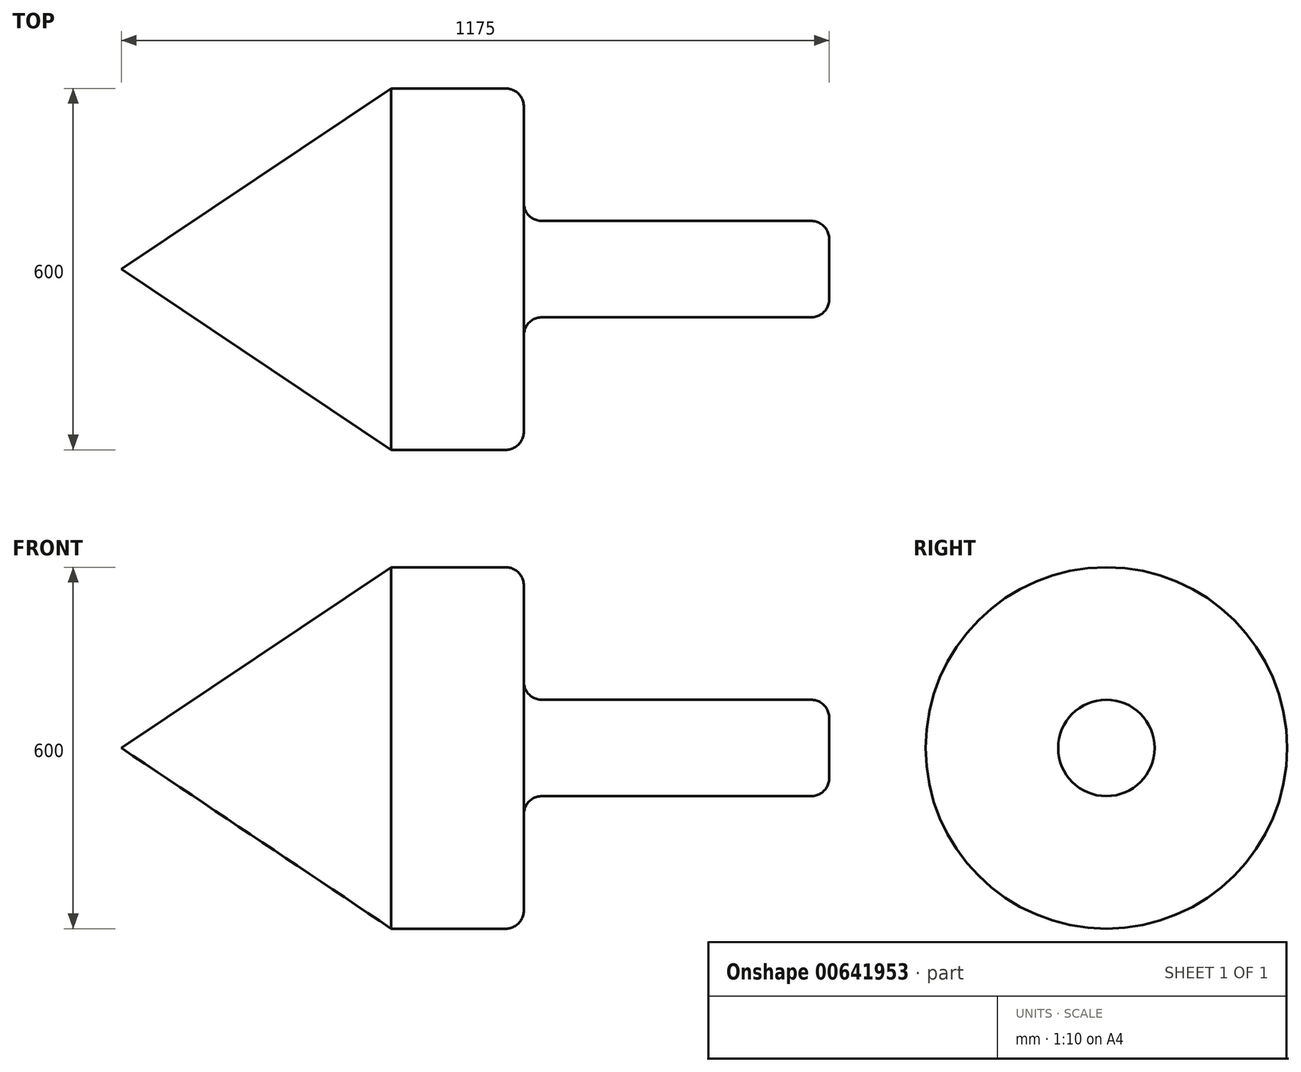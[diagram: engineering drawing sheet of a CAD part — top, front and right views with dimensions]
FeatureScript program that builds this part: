
annotation { "Feature Type Name" : "Feature", "Feature Type Description" : "" }
export const myFeature = defineFeature(function(context is Context, id is Id, definition is map)
    precondition{}
    {
        {
            var Q0;
            Q0=qCreatedBy(makeId("Front.planeOp"),FACE);
            var sketch = newSketch(context, id + "F0", { "sketchPlane" : qUnion([Q0])});
            skLineSegment(sketch, "E0", {"start": v(579.21, 0) * mm, "end": v(-595.79, 0) * mm});
            skLineSegment(sketch, "E1", {"start": v(579.21, 0) * mm, "end": v(579.21, 50) * mm});
            skLineSegment(sketch, "E2", {"start": v(549.21, 80) * mm, "end": v(102.21, 80) * mm});
            skLineSegment(sketch, "E3", {"start": v(72.21, 110) * mm, "end": v(72.21, 270) * mm});
            skLineSegment(sketch, "E4", {"start": v(42.21, 300) * mm, "end": v(-147.79, 300) * mm});
            skLineSegment(sketch, "E5", {"start": v(-147.79, 300) * mm, "end": v(-595.79, 0) * mm});
            skPoint(sketch, "E6.visualSharp", {"position": v(72.21, 300) * mm});
            skArc(sketch, "E6.filletArc", {"start": v(72.21, 270) * mm, "mid": v(63.43, 291.21) * mm, "end": v(42.21, 300) * mm});
            skPoint(sketch, "E7.visualSharp", {"position": v(72.21, 80) * mm});
            skArc(sketch, "E7.filletArc", {"start": v(72.21, 110) * mm, "mid": v(81, 88.79) * mm, "end": v(102.21, 80) * mm});
            skPoint(sketch, "E8.visualSharp", {"position": v(579.21, 80) * mm});
            skArc(sketch, "E8.filletArc", {"start": v(579.21, 50) * mm, "mid": v(570.43, 71.21) * mm, "end": v(549.21, 80) * mm});
            skSolve(sketch);
        }
        {
            var Q0;
            Q0 = qSketchRegion(id + "F0", true);
            var Q1;
            Q1=sQuery(id+"F0.wireOp",EDGE,"E0");
            revolve(context, id + "F1", {"entities" : qUnion([Q0]), "axis" : qUnion([Q1]), "revolveType" : RevolveType.FULL});
        }
    });
